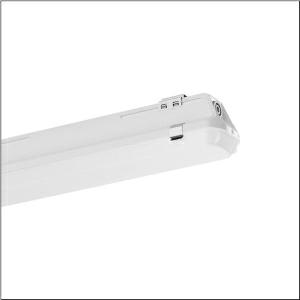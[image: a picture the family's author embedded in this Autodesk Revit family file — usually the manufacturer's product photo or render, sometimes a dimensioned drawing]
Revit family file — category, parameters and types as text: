
# Revit family: monsun_r__21_51fb207l440j005_68cc
name_source: partatom
category: Lighting Fixtures
units: mm (PartAtom-declared; Revit-internal decimal feet)

## family parameters
Cut with Voids When Loaded = No
Host = Face
Light Source = No
Part Type = Normal
Room Calculation Point = No
Round Connector Dimension = Use Diameter
Shared = No

## types (1)
- Monsun® 21 (1 x LED, 4410 lm, 29.8 W, 4000K)
    Apparent Load = 30 VA
    CIE Flux Codes = 45 75 93 94 100
    Color Rendering = 80
    Color Temperature = 4000K
    Default Elevation = 1800 mm
    Description = Monsun® 21, damp-proof luminaire, chain hanger, primary optical cover: enclosure, of PC, light emission: direct distribution, primary light characteristic: symmetric, installation type: suspended mounting, surface-mounted, horizontal mounting, vertical mounting, LED, rated luminous flux: 4.410lm, luminous efficacy: 147lm/W, light colour: 840, colour temperature: 4000K, control gear: ECG, with terminal, 3-pole, max. 2.5mm², through-wiring: 5x 2.5mm², mains connection: 220..240V, AC, 50/60Hz, rated input power: 30W, housing, of glass-fibre reinforced plastic, uncoated, bright grey, incl. chain hanger, length: 1.299mm, width: 90mm, height: 88mm, clip for enclosure, of stainless steel (V2A), ceiling mounting element, of stainless steel (V2A), chain hanger, of stainless steel (V2A), protection rating (complete): IP66, insulation class (complete): insulation class I (protective earthing), certification: CE, ENEC, VDE, UKCA, protection symbol: D, impact resistance: IK08, permissible operating ambient temperature: -25..+35°C, standard: EN 50419, EN 60598-2-1, corresponds to IFS (International Featured Standards) requirements for safety and quality in the food industry, for indoor or canopied outdoor use, no direct snow, no direct sun, no direct rain, contact your sales advisor before using the luminaires in applications with unclear chemical exposure, large temperature fluctuations or condensation-forming humidity, LABS conformity tested according to VDMA 24364:2018-05, packaging unit: 1 piece
    Height = 88 mm
    Lamp = 1 x LED
    Lamp Light Flux = 4410 lm
    Lamp Power = 29.8 W
    Lamp count = 1
    Length = 1299 mm
    Luminous efficacy = 148 lm/W
    Manufacturer = Siteco
    ModVariant = No
    Model = 51FB207L440J005
    Mounting Place = Ceiling
    Mounting Type = Surface mounted
    Number of Poles = 1
    OnlyDefault = Yes
    Power Factor = 1
    Product Name = Monsun® 21
    Product group = damp-proof luminaire
    ProductGroupID = 300
    Protection Class = Protection class I
    Protection Degree = IP 66
    RLX_Detail_Level = 1
    RLX_Emergency_Light_Flux = 0 lm
    RLX_Emergency_Type = 0
    RLX_Emergency_Type_DB = No
    RlxData = <blob elided: 89829 chars, md5=ee35d7ff>
    Socket = socket
    Standby Power = 0 W
    System Light Flux = 4410 lm
    System Power = 30 W
    Type Comments = Product without accessories
    Type Image = l_1006717.jpg
    URL = http://relux.com
    VarID = ---
    Voltage = 0 V
    Weight = 0.00 kg
    Width = 90 mm

## geometry (parser evidence)
native form markers: Blend x4, Sweep x12
no freeform markers — native parametric forms only
